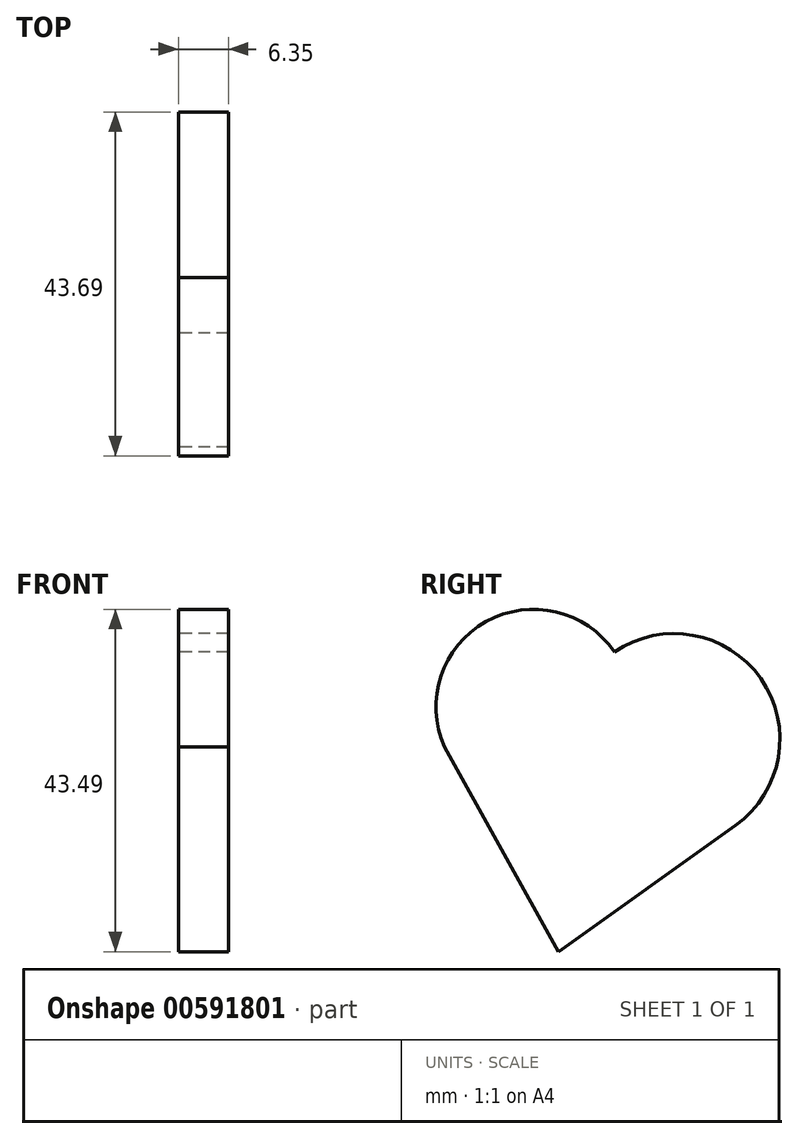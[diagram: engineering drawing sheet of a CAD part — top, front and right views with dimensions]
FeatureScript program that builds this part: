
annotation { "Feature Type Name" : "Feature", "Feature Type Description" : "" }
export const myFeature = defineFeature(function(context is Context, id is Id, definition is map)
    precondition{}
    {
        {
            var Q0;
            Q0=qCreatedBy(makeId("Right.planeOp"),FACE);
            var sketch = newSketch(context, id + "F0", { "sketchPlane" : qUnion([Q0])});
            skCircle(sketch, "E0", {"center": v(6.27, 19.8) * mm, "radius": 53.73 * mm});
            skCircle(sketch, "E1", {"center": v(-65.15, 36.26) * mm, "radius": 49.6 * mm});
            skLineSegment(sketch, "E2", {"start": v(-110.4, 15.96) * mm, "end": v(-52.48, -88.13) * mm});
            skLineSegment(sketch, "E3", {"start": v(-52.48, -88.13) * mm, "end": v(37.48, -23.93) * mm});
            skSolve(sketch);
        }
        {
            var Q0;
            {var subQ0=sQuery(id+"F0.wireOp",EDGE,"E2");var subQ1=sQuery(id+"F0.wireOp",EDGE,"E1");var subQ2=makeQuery(id+"F0.imprint","INTERSECT",VERTEX,{"disambiguationData":[OD(0.0)],"derivedFrom":[subQ1,subQ0]});Q0=makeQuery(id+"F0.imprint","IMPRINT",FACE,{"disambiguationData":[TD([[makeQuery(id+"F0.imprint","IMPRINT",EDGE,{"disambiguationData":[TD([[subQ2,-1.0]])],"derivedFrom":subQ1}),1.0]])]});}
            var Q1;
            {var subQ0=sQuery(id+"F0.wireOp",EDGE,"E1");var subQ1=sQuery(id+"F0.wireOp",EDGE,"E0");var subQ2=makeQuery(id+"F0.imprint","INTERSECT",VERTEX,{"disambiguationData":[OD(0.0)],"derivedFrom":[subQ1,subQ0]});Q1=makeQuery(id+"F0.imprint","IMPRINT",FACE,{"disambiguationData":[TD([[makeQuery(id+"F0.imprint","IMPRINT",EDGE,{"disambiguationData":[TD([[subQ2,-1.0]])],"derivedFrom":subQ1}),1.0]])]});}
            var Q2;
            {var subQ0=sQuery(id+"F0.wireOp",EDGE,"E3");Q2=makeQuery(id+"F0.imprint","IMPRINT",FACE,{"disambiguationData":[TD([[makeQuery(id+"F0.imprint","IMPRINT",EDGE,{"derivedFrom":subQ0}),1.0]])]});}
            var Q3;
            {var subQ0=sQuery(id+"F0.wireOp",EDGE,"E1");var subQ1=sQuery(id+"F0.wireOp",EDGE,"E0");var subQ2=makeQuery(id+"F0.imprint","INTERSECT",VERTEX,{"disambiguationData":[OD(0.0)],"derivedFrom":[subQ1,subQ0]});Q3=makeQuery(id+"F0.imprint","IMPRINT",FACE,{"disambiguationData":[TD([[makeQuery(id+"F0.imprint","IMPRINT",EDGE,{"disambiguationData":[TD([[subQ2,-1.0]])],"derivedFrom":subQ1}),-1.0]])]});}
            var Q4;
            {var subQ0=sQuery(id+"F0.wireOp",EDGE,"E0");var subQ1=makeQuery(id+"F0.imprint","INTERSECT",VERTEX,{"derivedFrom":[subQ0,sQuery(id+"F0.wireOp",EDGE,"E3")]});Q4=makeQuery(id+"F0.imprint","IMPRINT",FACE,{"disambiguationData":[TD([[makeQuery(id+"F0.imprint","IMPRINT",EDGE,{"disambiguationData":[TD([[subQ1,1.0]])],"derivedFrom":subQ0}),1.0]])]});}
            extrude(context, id + "F1", {"entities" : qUnion([Q0, Q1, Q2, Q3, Q4]), "depth" : 25.4 * mm, "offsetDistance" : 25.4 * mm});
        }
        {
            var Q0;
            Q0=makeQuery(id+"F1.opExtrude","SWEPT_BODY",BODY,{"disambiguationData":[OSD([sQuery(id+"F0.wireOp",EDGE,"E0"),sQuery(id+"F0.wireOp",EDGE,"E1"),sQuery(id+"F0.wireOp",EDGE,"E2"),sQuery(id+"F0.wireOp",EDGE,"E3")])]});
            var Q1;
            Q1=qCreatedBy(makeId("Origin.pointOp"),VERTEX);
            transform(context, id + "F2", {"entities" : qUnion([Q0]), "transformType" : TransformType.SCALE_UNIFORMLY, "scale" : .25, "scalePoint" : qUnion([Q1]), "makeCopy" : false});
        }
    });
